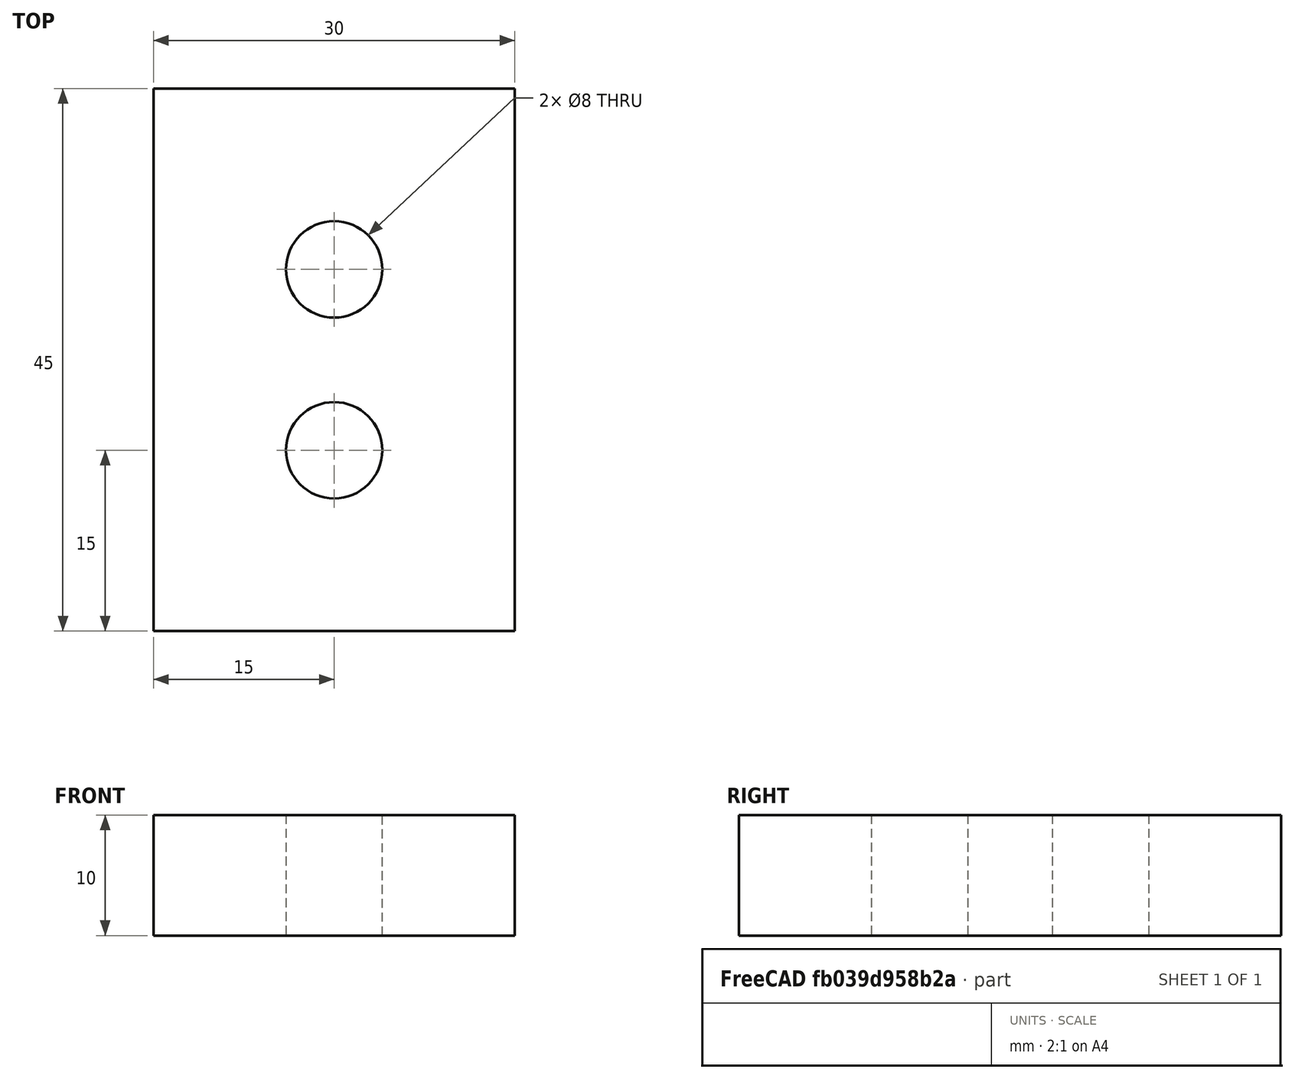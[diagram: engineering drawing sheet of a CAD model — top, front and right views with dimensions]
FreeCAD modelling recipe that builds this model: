
FCSTD DOCUMENT  (FreeCAD 0.19R)
Label: soporteSensor
License: All rights reserved
LicenseURL: http://en.wikipedia.org/wiki/All_rights_reserved
objects: Part::Extrusion×2, Sketcher::SketchObject×1
note: 3 computed .brp shape members not serialized (recipe doc carries the construction recipe); baked Part::Feature solids carry a one-line shape summary decoded from their .brp

FEATURE [Sketcher::SketchObject] Sketch
  FullyConstrained = true
  sketch-geometry (7):
    g0: LineSegment StartX=-15 StartY=15 StartZ=0 EndX=15 EndY=15 EndZ=0
    g1: LineSegment StartX=15 StartY=15 StartZ=0 EndX=15 EndY=-30 EndZ=0
    g2: LineSegment StartX=15 StartY=-30 StartZ=0 EndX=-15 EndY=-30 EndZ=0
    g3: LineSegment StartX=-15 StartY=-30 StartZ=0 EndX=-15 EndY=15 EndZ=0
    g4: Circle CenterX=0 CenterY=0 CenterZ=0 NormalX=0 NormalY=0 NormalZ=1 AngleXU=0 Radius=4
    g5: GeomPoint X=0 Y=-15 Z=0
    g6: Circle CenterX=0 CenterY=-15 CenterZ=0 NormalX=0 NormalY=0 NormalZ=1 AngleXU=0 Radius=4
  constraints (18):
    c: Coincident(g0,g1)
    c: Coincident(g1,g2)
    c: Coincident(g2,g3)
    c: Coincident(g3,g0)
    c: Horizontal(g0)
    c: Horizontal(g2)
    c: Vertical(g1)
    c: Vertical(g3)
    c: DistanceX(g0,g-1) = 15
    c: DistanceX(g-1,g0) = 15
    c: DistanceY(g-1,g0) = 15
    c: DistanceY(g1,g-1) = 30
    c: Radius(g4) = 4
    c: Coincident(g4,g-1)
    c: Vertical(g4,g5)
    c: DistanceY(g5,g4) = 15
    c: Radius(g6) = 4
    c: Coincident(g6,g5)
FEATURE [Part::Extrusion] Extrude
  Base = -> Sketch
  Dir = (0,0,1)
  DirMode = 2
  FaceMakerClass = Part::FaceMakerBullseye
  LengthFwd = 10
  LengthRev = 0
  Solid = true
  Symmetric = false
FEATURE [Part::Extrusion] Extrude001
  Base = -> Sketch
  Dir = (0,0,1)
  DirMode = 2
  FaceMakerClass = Part::FaceMakerBullseye
  LengthFwd = 10
  LengthRev = 0
  Solid = true
  Symmetric = false
